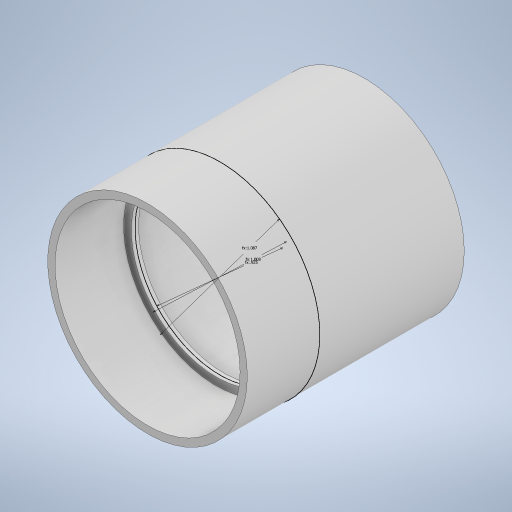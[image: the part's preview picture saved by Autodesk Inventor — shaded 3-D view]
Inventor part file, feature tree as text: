
AUTODESK INVENTOR PART (.ipt)
format: ipt  version: 2024 (Build 280153000, 153)  size: 238,080 bytes
history: native  units: in
note: dims shown in document units (in); Inventor stores cm internally (conversion verified against a paired STEP export)
features: extrude x2, sketch x1
ambient origin geometry x8: Origin, YZ Plane, XZ Plane, XY Plane, X Axis, Y Axis, Z Axis, Center Point
bodies: Solid1 (feature_tree)
feature tree (3):
  sketch  "Sketch1"  dims[d0=0.9252in d1=1.0079in d2=1.0866in d3=0.0394in d4=0.0in d5=0.3937in d6=0.7874in d7=0.0in d8=0.0in]
  extrude  "Extrusion1"  Depth=0.7874in
  extrude  "Extrusion2"  Depth=0.7874in
